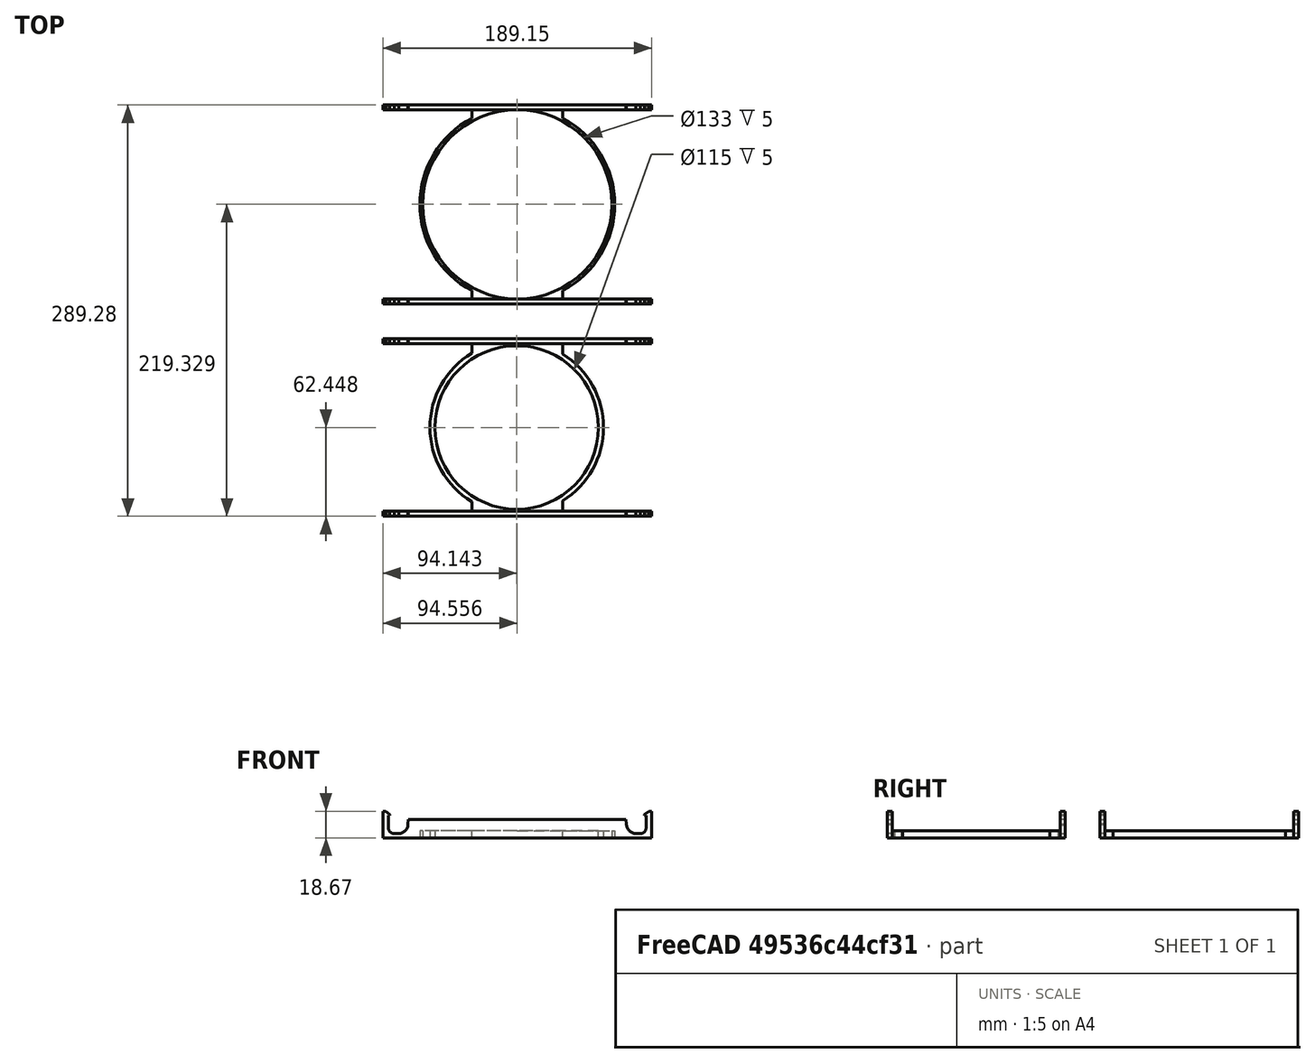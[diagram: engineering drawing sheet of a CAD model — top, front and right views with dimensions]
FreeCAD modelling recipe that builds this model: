
FCSTD DOCUMENT  (FreeCAD 0.20R29177 +426 (Git))
Label: round.container.hanger
License: All rights reserved
LicenseURL: http://en.wikipedia.org/wiki/All_rights_reserved
objects: Part::Extrusion×22, Part::Part2DObjectPython×20, Part::Refine×12, Part::MultiFuse×10, Part::Cut×7, Part::Feature×4
note: 75 computed .brp shape members not serialized (recipe doc carries the construction recipe); baked Part::Feature solids carry a one-line shape summary decoded from their .brp

FEATURE [Part::Part2DObjectPython] Circle  # Draft 2D object (typed FeaturePython)
  Area = 13892.9
  FirstAngle = 0
  LastAngle = 0
  MakeFace = true
  Placement = pos=(-1.94393,-264.211,-125.386) rot=(0.707107,0.707107,0;3.14159rad)
  Radius = 66.5
FEATURE [Part::Part2DObjectPython] Circle001  # Draft 2D object (typed FeaturePython)
  Area = 14313.9
  FirstAngle = 0
  LastAngle = 0
  MakeFace = true
  Placement = pos=(-1.94393,-264.211,-125.386) rot=(0.707107,0.707107,0;3.14159rad)
  Radius = 67.5
FEATURE [Part::Extrusion] Extrusion
  Base = -> Circle
  Dir = (1.61e-14,9.76e-14,5)
  DirMode = 0
  FaceMakerClass = Part::FaceMakerBullseye
  LengthFwd = 0
  LengthRev = 0
  Solid = true
  Symmetric = false
FEATURE [Part::Extrusion] Extrusion011
  Base = -> Circle001
  Dir = (1.61e-14,9.76e-14,5)
  DirMode = 0
  FaceMakerClass = Part::FaceMakerBullseye
  LengthFwd = 0
  LengthRev = 0
  Solid = true
  Symmetric = false
FEATURE [Part::Cut] Cut
  Base = -> Extrusion011
  Tool = -> Extrusion
FEATURE [Part::Refine] Slice007_child0001  label="Slice007.001"
  Placement = pos=(-77.6209,-78.2835,1.6627e-12) rot=(0,0,1;0rad)
FEATURE [Part::Refine] Slice007_child0002  label="Slice007.002"
  Placement = pos=(-77.6209,-214.733,4.8885e-12) rot=(0,0,1;0rad)
FEATURE [Part::MultiFuse] Fusion
  Shapes = -> [Slice007_child0002,Cut,Slice007_child0001]
FEATURE [Part::Part2DObjectPython] Circle002  # Draft 2D object (typed FeaturePython)
  Area = 13892.9
  FirstAngle = 0
  LastAngle = 0
  MakeFace = true
  Placement = pos=(-1.94393,-264.211,-125.386) rot=(-0.707107,0.707107,0;3.14159rad)
  Radius = 66.5
FEATURE [Part::Part2DObjectPython] Circle003  # Draft 2D object (typed FeaturePython)
  Area = 14741.1
  FirstAngle = 0
  LastAngle = 0
  MakeFace = true
  Placement = pos=(-1.94393,-264.211,-125.386) rot=(-0.707107,0.707107,0;3.14159rad)
  Radius = 68.5
FEATURE [Part::Extrusion] Extrusion012
  Base = -> Circle002
  Dir = (1.7e-14,9.63e-14,5)
  DirMode = 0
  FaceMakerClass = Part::FaceMakerBullseye
  LengthFwd = 0
  LengthRev = 0
  Solid = true
  Symmetric = false
FEATURE [Part::Extrusion] Extrusion013
  Base = -> Circle003
  Dir = (1.7e-14,9.63e-14,5)
  DirMode = 0
  FaceMakerClass = Part::FaceMakerBullseye
  LengthFwd = 0
  LengthRev = 0
  Solid = true
  Symmetric = false
FEATURE [Part::Cut] Cut001
  Base = -> Extrusion013
  Tool = -> Extrusion012
FEATURE [Part::MultiFuse] Fusion001
  Shapes = -> [Cut001,Fusion]
FEATURE [Part::Refine] Fusion001001
  Source = -> Fusion001
FEATURE [Part::Part2DObjectPython] Wire  # Draft 2D object (typed FeaturePython)
  Area = 45.742
  ChamferSize = 0
  Closed = true
  End = (-33.8804,-324.81,-125.386)
  FilletRadius = 0
  Length = 37.9946
  MakeFace = true
  Placement = pos=(-18.3756,-330.711,-125.386) rot=(1,0,0;3.14159rad)
  Points = (3) [(0,0,0),(-15.5048,3.97904e-13,-4.26326e-14),(-15.5048,-5.90038,2.84217e-14)]
  Start = (-18.3756,-330.711,-125.386)
  Subdivisions = 0
FEATURE [Part::Part2DObjectPython] Wire001  # Draft 2D object (typed FeaturePython)
  Area = 45.742
  ChamferSize = 0
  Closed = true
  End = (-18.3756,-197.711,-125.386)
  FilletRadius = 0
  Length = 37.9946
  MakeFace = true
  Placement = pos=(-33.8804,-197.711,-125.386) rot=(1,0,0;3.14159rad)
  Points = (3) [(0,0,0),(-7.10543e-15,5.90038,4.26326e-14),(15.5048,1.7053e-13,0)]
  Start = (-33.8804,-197.711,-125.386)
  Subdivisions = 0
FEATURE [Part::Part2DObjectPython] Wire002  # Draft 2D object (typed FeaturePython)
  Area = 46.1906
  ChamferSize = 0
  Closed = true
  End = (30.0561,-203.645,-125.386)
  FilletRadius = 0
  Length = 38.1631
  MakeFace = true
  Placement = pos=(14.4878,-197.711,-125.386) rot=(1,0,0;3.14159rad)
  Points = (3) [(0,0,0),(15.5683,0,2.84217e-13),(15.5683,5.93392,-2.84217e-14)]
  Start = (14.4878,-197.711,-125.386)
  Subdivisions = 0
FEATURE [Part::Part2DObjectPython] Wire003  # Draft 2D object (typed FeaturePython)
  Area = 46.1906
  ChamferSize = 0
  Closed = true
  End = (30.0561,-324.777,-125.386)
  FilletRadius = 0
  Length = 38.1631
  MakeFace = true
  Placement = pos=(14.4878,-330.711,-125.386) rot=(1,0,0;3.14159rad)
  Points = (3) [(0,0,0),(15.5683,3.97904e-13,4.26326e-14),(15.5683,-5.93392,-5.68434e-14)]
  Start = (14.4878,-330.711,-125.386)
  Subdivisions = 0
FEATURE [Part::Extrusion] Extrusion014
  Base = -> Wire003
  Dir = (3.96e-14,3.25e-14,5)
  DirMode = 0
  FaceMakerClass = Part::FaceMakerBullseye
  LengthFwd = 0
  LengthRev = 0
  Solid = true
  Symmetric = false
FEATURE [Part::Extrusion] Extrusion015
  Base = -> Wire002
  Dir = (1.171e-13,3.797e-13,5)
  DirMode = 0
  FaceMakerClass = Part::FaceMakerBullseye
  LengthFwd = 0
  LengthRev = 0
  Solid = true
  Symmetric = false
FEATURE [Part::Extrusion] Extrusion016
  Base = -> Wire
  Dir = (3.96e-14,1.765e-13,5)
  DirMode = 0
  FaceMakerClass = Part::FaceMakerBullseye
  LengthFwd = 0
  LengthRev = 0
  Solid = true
  Symmetric = false
FEATURE [Part::Extrusion] Extrusion017
  Base = -> Wire001
  Dir = (2.59e-14,8.02e-14,5)
  DirMode = 0
  FaceMakerClass = Part::FaceMakerBullseye
  LengthFwd = 0
  LengthRev = 0
  Solid = true
  Symmetric = false
FEATURE [Part::MultiFuse] Fusion001002
  Shapes = -> [Extrusion017,Extrusion015,Extrusion016,Extrusion014,Fusion001001]
FEATURE [Part::Refine] Fusion001002001
  Source = -> Fusion001002
FEATURE [Part::Part2DObjectPython] Rectangle  # Draft 2D object (typed FeaturePython)
  Area = 8.92715
  ChamferSize = 0
  Columns = 1
  FilletRadius = 0
  Height = 4.46358
  Length = 2
  MakeFace = true
  Placement = pos=(-96.5002,-194.261,-120.923) rot=(-1,0,0;1.5708rad)
  Rows = 1
FEATURE [Part::Extrusion] Extrusion018
  Base = -> Rectangle
  Dir = (-2.58e-14,-3.45,4.244e-13)
  DirMode = 0
  FaceMakerClass = Part::FaceMakerBullseye
  LengthFwd = 0
  LengthRev = 0
  Placement = pos=(187.113,-136.45,2.7711e-12) rot=(0,0,1;0rad)
  Solid = true
  Symmetric = false
FEATURE [Part::Part2DObjectPython] Rectangle001  # Draft 2D object (typed FeaturePython)
  Area = 8.92715
  ChamferSize = 0
  Columns = 1
  FilletRadius = 0
  Height = 4.46358
  Length = 2
  MakeFace = true
  Placement = pos=(-96.5002,-194.261,-120.923) rot=(-1,0,0;1.5708rad)
  Rows = 1
FEATURE [Part::Extrusion] Extrusion019
  Base = -> Rectangle001
  Dir = (-2.58e-14,-3.45,4.244e-13)
  DirMode = 0
  FaceMakerClass = Part::FaceMakerBullseye
  LengthFwd = 0
  LengthRev = 0
  Placement = pos=(-1.6868e-11,-136.45,4.3116e-11) rot=(0,0,1;0rad)
  Solid = true
  Symmetric = false
FEATURE [Part::Part2DObjectPython] Rectangle002  # Draft 2D object (typed FeaturePython)
  Area = 8.92715
  ChamferSize = 0
  Columns = 1
  FilletRadius = 0
  Height = 4.46358
  Length = 2
  MakeFace = true
  Placement = pos=(-96.5002,-194.261,-120.923) rot=(-1,0,0;1.5708rad)
  Rows = 1
FEATURE [Part::Extrusion] Extrusion020
  Base = -> Rectangle002
  Dir = (-2.58e-14,-3.45,4.244e-13)
  DirMode = 0
  FaceMakerClass = Part::FaceMakerBullseye
  LengthFwd = 0
  LengthRev = 0
  Placement = pos=(-1.85e-13,0,8.24e-13) rot=(0,0,1;0rad)
  Solid = true
  Symmetric = false
FEATURE [Part::Part2DObjectPython] Rectangle003  # Draft 2D object (typed FeaturePython)
  Area = 8.92715
  ChamferSize = 0
  Columns = 1
  FilletRadius = 0
  Height = 4.46358
  Length = 2
  MakeFace = true
  Placement = pos=(-96.5002,-194.261,-120.923) rot=(-1,0,0;1.5708rad)
  Rows = 1
FEATURE [Part::Extrusion] Extrusion021
  Base = -> Rectangle003
  Dir = (-2.58e-14,-3.45,4.244e-13)
  DirMode = 0
  FaceMakerClass = Part::FaceMakerBullseye
  LengthFwd = 0
  LengthRev = 0
  Placement = pos=(187.113,2.27e-13,-4.55e-13) rot=(0,0,1;0rad)
  Solid = true
  Symmetric = false
FEATURE [Part::MultiFuse] Fusion001002002
  Shapes = -> [Extrusion018,Fusion001002001,Extrusion019]
FEATURE [Part::Refine] Fusion001002002001
  Source = -> Fusion001002002
FEATURE [Part::MultiFuse] Fusion001002002002
  Shapes = -> [Extrusion021,Fusion001002002001,Extrusion020]
FEATURE [Part::Refine] Fusion001002002002001
  Source = -> Fusion001002002002
FEATURE [Part::Feature] Face
  shape: bbox 0.9932 x 3.45 x 0.000473 mm, 1 faces, 0 solids (baked)
FEATURE [Part::Extrusion] Extrusion022
  Base = -> Face
  Dir = (-1e-16,-5.491e-13,-4.46358)
  DirMode = 0
  FaceMakerClass = Part::FaceMakerBullseye
  LengthFwd = 0
  LengthRev = 0
  Solid = true
  Symmetric = false
FEATURE [Part::Cut] Cut002
  Base = -> Fusion001002002002001
  Tool = -> Extrusion022
FEATURE [Part::Part2DObjectPython] Rectangle005  # Draft 2D object (typed FeaturePython)
  Area = 64.384
  ChamferSize = 0
  Columns = 1
  FilletRadius = 0
  Height = 18.662
  Length = 3.45
  MakeFace = true
  Placement = pos=(-96.5002,-194.261,-125.386) rot=(0.57735,-0.57735,-0.57735;2.0944rad)
  Rows = 1
FEATURE [Part::Extrusion] Extrusion023
  Base = -> Rectangle005
  Dir = (1.48965,5e-16,8.7e-15)
  DirMode = 0
  FaceMakerClass = Part::FaceMakerBullseye
  LengthFwd = 0
  LengthRev = 0
  Solid = true
  Symmetric = false
FEATURE [Part::MultiFuse] Fusion001002002002002
  Shapes = -> [Cut002,Extrusion023]
FEATURE [Part::Refine] Fusion001002002002002001
  Source = -> Fusion001002002002002
FEATURE [Part::Feature] Face001
  shape: bbox 0.9932 x 3.45 x 0.000473 mm, 1 faces, 0 solids (baked)
FEATURE [Part::Extrusion] Extrusion024
  Base = -> Face001
  Dir = (-1e-16,-5.491e-13,-4.46358)
  DirMode = 0
  FaceMakerClass = Part::FaceMakerBullseye
  LengthFwd = 0
  LengthRev = 0
  Solid = true
  Symmetric = false
FEATURE [Part::Cut] Cut003
  Base = -> Fusion001002002002002001
  Tool = -> Extrusion024
FEATURE [Part::Part2DObjectPython] Rectangle006  # Draft 2D object (typed FeaturePython)
  Area = 64.3916
  ChamferSize = 0
  Columns = 1
  FilletRadius = 0
  Height = 18.6642
  Length = 3.45
  MakeFace = true
  Placement = pos=(-96.5002,-330.711,-125.386) rot=(-0.57735,0.57735,0.57735;4.18879rad)
  Rows = 1
FEATURE [Part::Extrusion] Extrusion025
  Base = -> Rectangle006
  Dir = (1.48965,-1.694e-13,1.69e-13)
  DirMode = 0
  FaceMakerClass = Part::FaceMakerBullseye
  LengthFwd = 0
  LengthRev = 0
  Solid = true
  Symmetric = false
FEATURE [Part::MultiFuse] Fusion001002002002002002
  Shapes = -> [Cut003,Extrusion025]
FEATURE [Part::Refine] Fusion001002002002002002001
  Source = -> Fusion001002002002002002
FEATURE [Part::Feature] Face002
  shape: bbox 0.9932 x 3.45 x 0.000473 mm, 1 faces, 0 solids (baked)
FEATURE [Part::Extrusion] Extrusion026
  Base = -> Face002
  Dir = (-1e-16,-5.491e-13,-4.46358)
  DirMode = 0
  FaceMakerClass = Part::FaceMakerBullseye
  LengthFwd = 0
  LengthRev = 0
  Solid = true
  Symmetric = false
FEATURE [Part::Cut] Cut004
  Base = -> Fusion001002002002002002001
  Tool = -> Extrusion026
FEATURE [Part::Part2DObjectPython] Rectangle007  # Draft 2D object (typed FeaturePython)
  Area = 64.3914
  ChamferSize = 0
  Columns = 1
  FilletRadius = 0
  Height = 18.6642
  Length = 3.45
  MakeFace = true
  Placement = pos=(92.6124,-330.711,-106.722) rot=(-0.576947,0.576947,-0.578156;2.09319rad)
  Rows = 1
FEATURE [Part::Extrusion] Extrusion027
  Base = -> Rectangle007
  Dir = (-1.48964,-7.08e-14,-0.00312006)
  DirMode = 0
  FaceMakerClass = Part::FaceMakerBullseye
  LengthFwd = 0
  LengthRev = 0
  Solid = true
  Symmetric = false
FEATURE [Part::MultiFuse] Fusion001002002002002002002
  Shapes = -> [Cut004,Extrusion027]
FEATURE [Part::Refine] Fusion001002002002002002002001
  Source = -> Fusion001002002002002002002
FEATURE [Part::Feature] Face003
  shape: bbox 0.9932 x 3.45 x 0.000473 mm, 1 faces, 0 solids (baked)
FEATURE [Part::Extrusion] Extrusion028
  Base = -> Face003
  Dir = (-1e-16,-5.491e-13,-4.46358)
  DirMode = 0
  FaceMakerClass = Part::FaceMakerBullseye
  LengthFwd = 0
  LengthRev = 0
  Solid = true
  Symmetric = false
FEATURE [Part::Cut] Cut005
  Base = -> Fusion001002002002002002002001
  Tool = -> Extrusion028
FEATURE [Part::Part2DObjectPython] Rectangle008  # Draft 2D object (typed FeaturePython)
  Area = 64.3914
  ChamferSize = 0
  Columns = 1
  FilletRadius = 0
  Height = 18.6642
  Length = 3.45
  MakeFace = true
  Placement = pos=(92.5733,-194.261,-106.722) rot=(-0.576947,0.576947,-0.578156;2.09319rad)
  Rows = 1
FEATURE [Part::Extrusion] Extrusion029
  Base = -> Rectangle008
  Dir = (-1.45055,-7.09e-14,-0.00303818)
  DirMode = 0
  FaceMakerClass = Part::FaceMakerBullseye
  LengthFwd = 0
  LengthRev = 0
  Solid = true
  Symmetric = false
FEATURE [Part::MultiFuse] Fusion001002002002002002002002
  Shapes = -> [Cut005,Extrusion029]
FEATURE [Part::Refine] Fusion001002002002002002002002001
  Source = -> Fusion001002002002002002002002
FEATURE [Part::Refine] Fusion001002002002002002002002001002001
  Placement = pos=(0,-156.881,3.0695e-12) rot=(0,0,1;0rad)
FEATURE [Part::Part2DObjectPython] ShapeString  # Draft 2D object (typed FeaturePython)
  FontFile = /run/user/1000/doc/f5ed1d15/Futura Bold font.ttf
  MakeFace = true
  Placement = pos=(145.492,-424.213,-125.386) rot=(0,0,1;0rad)
  Size = 10
  String = 118 mm brown
  Tracking = 0
FEATURE [Part::Part2DObjectPython] ShapeString001  # Draft 2D object (typed FeaturePython)
  FontFile = /run/user/1000/doc/f5ed1d15/Futura Bold font.ttf
  MakeFace = true
  Placement = pos=(132.164,-267.102,-125.386) rot=(0,0,1;0rad)
  Size = 10
  String = 133 mm gray
  Tracking = 0
FEATURE [Part::Part2DObjectPython] Circle004  # Draft 2D object (typed FeaturePython)
  Area = 11309.7
  FirstAngle = 0
  LastAngle = 0
  MakeFace = true
  Placement = pos=(-2.35676,-421.092,-125.386) rot=(1,0,0;3.14159rad)
  Radius = 60
FEATURE [Part::Part2DObjectPython] Circle005  # Draft 2D object (typed FeaturePython)
  Area = 10386.9
  FirstAngle = 0
  LastAngle = 0
  MakeFace = true
  Placement = pos=(-2.35676,-421.092,-125.386) rot=(1,0,0;3.14159rad)
  Radius = 57.5
FEATURE [Part::Extrusion] Extrusion030
  Base = -> Circle004
  Dir = (-7.51e-14,2.785e-13,5)
  DirMode = 0
  FaceMakerClass = Part::FaceMakerBullseye
  LengthFwd = 0
  LengthRev = 0
  Solid = true
  Symmetric = false
FEATURE [Part::Extrusion] Extrusion031
  Base = -> Circle005
  Dir = (-7.51e-14,2.785e-13,5)
  DirMode = 0
  FaceMakerClass = Part::FaceMakerBullseye
  LengthFwd = 0
  LengthRev = 0
  Solid = true
  Symmetric = false
FEATURE [Part::Cut] Cut006
  Base = -> Extrusion030
  Tool = -> Extrusion031
FEATURE [Part::MultiFuse] Fusion001002002002002002002002001002002
  Shapes = -> [Cut006,Fusion001002002002002002002002001002001]
FEATURE [Part::Refine] Fusion001002002002002002002002001002002001
  Source = -> Fusion001002002002002002002002001002002
